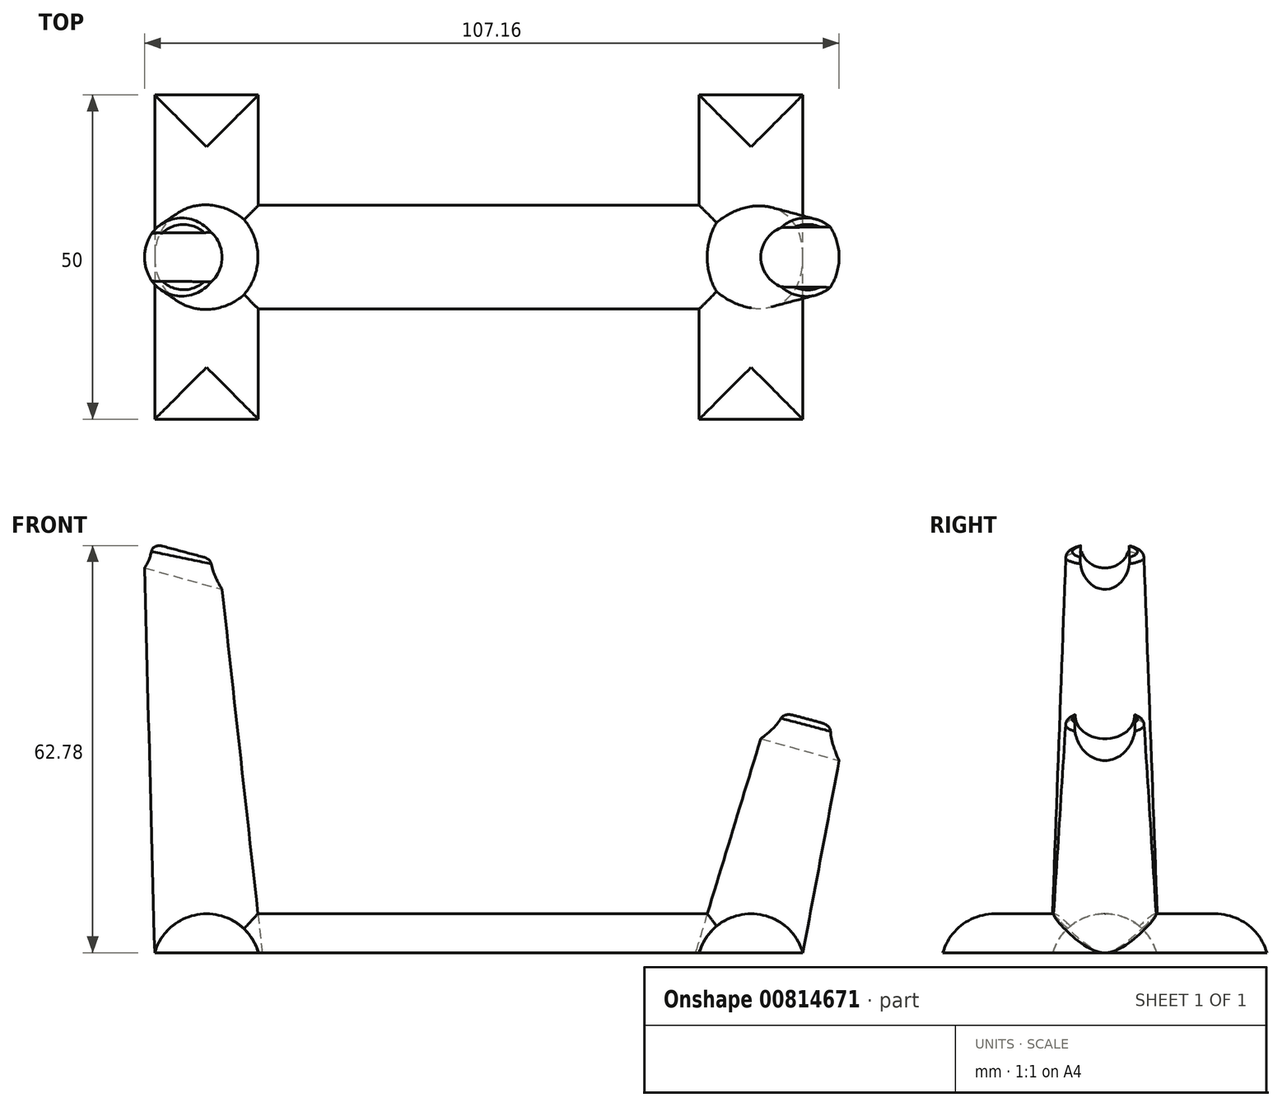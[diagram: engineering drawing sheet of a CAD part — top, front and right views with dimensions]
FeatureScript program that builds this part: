
annotation { "Feature Type Name" : "Feature", "Feature Type Description" : "" }
export const myFeature = defineFeature(function(context is Context, id is Id, definition is map)
    precondition{}
    {
        {
            var Q0;
            Q0=qCreatedBy(makeId("Top.planeOp"),FACE);
            var sketch = newSketch(context, id + "F0", { "sketchPlane" : qUnion([Q0])});
            skLineSegment(sketch, "E0.bottom", {"start": v(-50, 8) * mm, "end": v(50, 8) * mm});
            skLineSegment(sketch, "E0.top", {"start": v(-50, -8) * mm, "end": v(50, -8) * mm});
            skLineSegment(sketch, "E0.left", {"start": v(-50, 8) * mm, "end": v(-50, -8) * mm});
            skLineSegment(sketch, "E0.right", {"start": v(50, 8) * mm, "end": v(50, -8) * mm});
            skPoint(sketch, "E0.middle", {"position": v(0, 0) * mm});
            skLineSegment(sketch, "E1.bottom", {"start": v(-50, 25) * mm, "end": v(-34, 25) * mm});
            skLineSegment(sketch, "E1.top", {"start": v(-50, -25) * mm, "end": v(-34, -25) * mm});
            skLineSegment(sketch, "E1.left", {"start": v(-50, 25) * mm, "end": v(-50, -25) * mm});
            skLineSegment(sketch, "E1.right", {"start": v(-34, 25) * mm, "end": v(-34, -25) * mm});
            skLineSegment(sketch, "E2.bottom", {"start": v(50, -25) * mm, "end": v(34, -25) * mm});
            skLineSegment(sketch, "E2.top", {"start": v(50, 25) * mm, "end": v(34, 25) * mm});
            skLineSegment(sketch, "E2.left", {"start": v(50, -25) * mm, "end": v(50, 25) * mm});
            skLineSegment(sketch, "E2.right", {"start": v(34, -25) * mm, "end": v(34, 25) * mm});
            skPoint(sketch, "E3", {"position": v(-34, 0) * mm});
            skPoint(sketch, "E4", {"position": v(-50, 0) * mm});
            skPoint(sketch, "E5", {"position": v(34, 0) * mm});
            skSolve(sketch);
        }
        {
            var Q0;
            Q0 = qSketchRegion(id + "F0", true);
            extrude(context, id + "F1", {"entities" : qUnion([Q0]), "depth" : 6 * mm, "offsetDistance" : 25 * mm});
        }
        {
            var Q0;
            Q0=makeQuery(id+"F1.opExtrude","CAP_FACE",FACE,{"disambiguationData":[OSD([sQuery(id+"F0.wireOp",EDGE,"E0.bottom"),sQuery(id+"F0.wireOp",EDGE,"E0.top"),sQuery(id+"F0.wireOp",EDGE,"E1.bottom"),sQuery(id+"F0.wireOp",EDGE,"E1.top"),sQuery(id+"F0.wireOp",EDGE,"E1.left"),sQuery(id+"F0.wireOp",EDGE,"E1.right"),sQuery(id+"F0.wireOp",EDGE,"E2.bottom"),sQuery(id+"F0.wireOp",EDGE,"E2.top"),sQuery(id+"F0.wireOp",EDGE,"E2.left"),sQuery(id+"F0.wireOp",EDGE,"E2.right")])],"isStart":false});
            fillet(context, id + "F2", {"entities" : qUnion([Q0]), "radius" : 8.3 * mm, "tangentPropagation" : true, "allowEdgeOverflow" : false});
        }
        {
            var Q0;
            {var subQ0=sQuery(id+"F0.wireOp",EDGE,"E2.left");Q0=makeQuery(id+"F2.opFillet","BLEND_EDGE",EDGE,{"blendedFrom":[makeQuery(id+"F1.opExtrude","CAP_EDGE",EDGE,{"disambiguationData":[OSD([subQ0])],"isStart":false}),makeQuery(id+"F1.opExtrude","CAP_FACE",FACE,{"disambiguationData":[OSD([sQuery(id+"F0.wireOp",EDGE,"E0.bottom"),sQuery(id+"F0.wireOp",EDGE,"E0.top"),sQuery(id+"F0.wireOp",EDGE,"E1.bottom"),sQuery(id+"F0.wireOp",EDGE,"E1.top"),sQuery(id+"F0.wireOp",EDGE,"E1.left"),sQuery(id+"F0.wireOp",EDGE,"E1.right"),sQuery(id+"F0.wireOp",EDGE,"E2.bottom"),sQuery(id+"F0.wireOp",EDGE,"E2.top"),subQ0,sQuery(id+"F0.wireOp",EDGE,"E2.right")])],"isStart":true})],"blendedInto":[makeQuery(id+"F1.opExtrude","CAP_FACE",FACE,{"disambiguationData":[OSD([sQuery(id+"F0.wireOp",EDGE,"E0.bottom"),sQuery(id+"F0.wireOp",EDGE,"E0.top"),sQuery(id+"F0.wireOp",EDGE,"E1.bottom"),sQuery(id+"F0.wireOp",EDGE,"E1.top"),sQuery(id+"F0.wireOp",EDGE,"E1.left"),sQuery(id+"F0.wireOp",EDGE,"E1.right"),sQuery(id+"F0.wireOp",EDGE,"E2.bottom"),sQuery(id+"F0.wireOp",EDGE,"E2.top"),subQ0,sQuery(id+"F0.wireOp",EDGE,"E2.right")])],"isStart":true})]});}
            cPlane(context, id + "F3", {"entities" : qUnion([Q0]), "cplaneType" : CPlaneType.LINE_ANGLE, "offset" : 25 * mm, "angle" : 15 * degree, "width" : 150 * mm, "height" : 150 * mm});
        }
        {
            var Q0;
            Q0=qCreatedBy(id+"F3.planeOp",FACE);
            cPlane(context, id + "F4", {"entities" : qUnion([Q0]), "cplaneType" : CPlaneType.OFFSET, "offset" : 35 * mm, "width" : 150 * mm, "height" : 150 * mm});
        }
        {
            var Q0;
            Q0=makeQuery(id+"F1.opExtrude","CAP_FACE",FACE,{"disambiguationData":[OSD([sQuery(id+"F0.wireOp",EDGE,"E0.bottom"),sQuery(id+"F0.wireOp",EDGE,"E0.top"),sQuery(id+"F0.wireOp",EDGE,"E1.bottom"),sQuery(id+"F0.wireOp",EDGE,"E1.top"),sQuery(id+"F0.wireOp",EDGE,"E1.left"),sQuery(id+"F0.wireOp",EDGE,"E1.right"),sQuery(id+"F0.wireOp",EDGE,"E2.bottom"),sQuery(id+"F0.wireOp",EDGE,"E2.top"),sQuery(id+"F0.wireOp",EDGE,"E2.left"),sQuery(id+"F0.wireOp",EDGE,"E2.right")])],"isStart":true});
            var sketch = newSketch(context, id + "F5", { "sketchPlane" : qUnion([Q0])});
            skCircle(sketch, "E6", {"center": v(-41.7, 0) * mm, "radius": 8.3 * mm});
            skCircle(sketch, "E7", {"center": v(41.7, 0) * mm, "radius": 8.3 * mm});
            skPoint(sketch, "E8", {"position": v(-50, 0) * mm});
            skPoint(sketch, "E9", {"position": v(50, 0) * mm});
            skSolve(sketch);
        }
        {
            var Q0;
            Q0=qCreatedBy(id+"F4.planeOp",FACE);
            var sketch = newSketch(context, id + "F6", { "sketchPlane" : qUnion([Q0])});
            skCircle(sketch, "E10", {"center": v(-60.35, 0) * mm, "radius": 6 * mm});
            skCircle(sketch, "E11", {"center": v(39.65, 0) * mm, "radius": 6 * mm});
            skPoint(sketch, "E12", {"position": v(-66.35, 0) * mm});
            skPoint(sketch, "E13", {"position": v(45.65, 0) * mm});
            skLineSegment(sketch, "E14", {"start": v(-60.35, 0) * mm, "end": v(-10.35, 0) * mm, "construction": true});
            skLineSegment(sketch, "E15", {"start": v(-10.35, 0) * mm, "end": v(39.65, 0) * mm, "construction": true});
            skSolve(sketch);
        }
        {
            var Q1;
            Q1=makeQuery(id+"F6.imprint","IMPRINT",FACE,{"disambiguationData":[TD([[makeQuery(id+"F6.imprint","IMPRINT",EDGE,{"derivedFrom":sQuery(id+"F6.wireOp",EDGE,"E10")}),1.0]])]});
            var Q2;
            Q2=makeQuery(id+"F5.imprint","IMPRINT",FACE,{"disambiguationData":[TD([[makeQuery(id+"F5.imprint","IMPRINT",EDGE,{"derivedFrom":sQuery(id+"F5.wireOp",EDGE,"E6")}),1.0]])]});
            var Q3;
            Q3=sQuery(id+"F5.wireOp",VERTEX,"E8");
            var Q4;
            Q4=sQuery(id+"F6.wireOp",VERTEX,"E12");
            loft(context, id + "F7", {"operationType" : NewBodyOperationType.ADD, "sheetProfilesArray" : [{ "sheetProfileEntities" : qUnion([Q1]) }, { "sheetProfileEntities" : qUnion([Q2]) }], "matchConnections" : true, "connections" : [{ "connectionEntities" : qUnion([Q3, Q4]), "connectionEdgeQueries" : qUnion([]), "connectionEdgeParameters" : [] }]});
        }
        {
            var Q1;
            Q1=makeQuery(id+"F6.imprint","IMPRINT",FACE,{"disambiguationData":[TD([[makeQuery(id+"F6.imprint","IMPRINT",EDGE,{"derivedFrom":sQuery(id+"F6.wireOp",EDGE,"E11")}),1.0]])]});
            var Q2;
            Q2=makeQuery(id+"F5.imprint","IMPRINT",FACE,{"disambiguationData":[TD([[makeQuery(id+"F5.imprint","IMPRINT",EDGE,{"derivedFrom":sQuery(id+"F5.wireOp",EDGE,"E7")}),1.0]])]});
            var Q3;
            Q3=sQuery(id+"F5.wireOp",VERTEX,"E9");
            var Q4;
            Q4=sQuery(id+"F6.wireOp",VERTEX,"E13");
            loft(context, id + "F8", {"operationType" : NewBodyOperationType.ADD, "sheetProfilesArray" : [{ "sheetProfileEntities" : qUnion([Q1]) }, { "sheetProfileEntities" : qUnion([Q2]) }], "matchConnections" : true, "connections" : [{ "connectionEntities" : qUnion([Q3, Q4]), "connectionEdgeQueries" : qUnion([]), "connectionEdgeParameters" : [] }]});
        }
        {
            var Q0;
            Q0=makeQuery(id+"F7.opLoft","CAP_FACE",FACE,{"disambiguationData":[OSD([makeQuery(id+"F6.imprint","IMPRINT",FACE,{"disambiguationData":[TD([[makeQuery(id+"F6.imprint","IMPRINT",EDGE,{"derivedFrom":sQuery(id+"F6.wireOp",EDGE,"E10")}),1.0]])]})])],"isStart":true});
            var sketch = newSketch(context, id + "F9", { "sketchPlane" : qUnion([Q0])});
            skLineSegment(sketch, "E16.bottom", {"start": v(35.97, 4.74) * mm, "end": v(54.64, 4.74) * mm});
            skLineSegment(sketch, "E16.top", {"start": v(35.97, -4.79) * mm, "end": v(54.64, -4.79) * mm});
            skLineSegment(sketch, "E16.left", {"start": v(35.97, 4.74) * mm, "end": v(35.97, -4.79) * mm});
            skLineSegment(sketch, "E16.right", {"start": v(54.64, 4.74) * mm, "end": v(54.64, -4.79) * mm});
            skPoint(sketch, "E17", {"position": v(35.97, -0.03) * mm});
            skLineSegment(sketch, "E18.bottom", {"start": v(35.97, 4.74) * mm, "end": v(31.93, 4.74) * mm});
            skLineSegment(sketch, "E18.top", {"start": v(35.97, -4.79) * mm, "end": v(31.93, -4.79) * mm});
            skLineSegment(sketch, "E18.right", {"start": v(31.93, 4.74) * mm, "end": v(31.93, -4.79) * mm});
            skLineSegment(sketch, "E19.bottom", {"start": v(-55.64, 3.72) * mm, "end": v(-81.84, 3.72) * mm});
            skLineSegment(sketch, "E19.top", {"start": v(-55.64, -3.77) * mm, "end": v(-81.84, -3.77) * mm});
            skLineSegment(sketch, "E19.left", {"start": v(-55.64, 3.72) * mm, "end": v(-55.64, -3.77) * mm});
            skLineSegment(sketch, "E19.right", {"start": v(-81.84, 3.72) * mm, "end": v(-81.84, -3.77) * mm});
            skLineSegment(sketch, "E20.bottom", {"start": v(-60.2, 3.72) * mm, "end": v(-55.64, 3.72) * mm});
            skLineSegment(sketch, "E20.top", {"start": v(-60.2, -3.77) * mm, "end": v(-55.64, -3.77) * mm});
            skLineSegment(sketch, "E20.right", {"start": v(-60.2, 3.72) * mm, "end": v(-60.2, -3.77) * mm});
            skPoint(sketch, "E21", {"position": v(-81.84, -0.03) * mm});
            skSolve(sketch);
        }
        {
            var Q0;
            Q0=sQuery(id+"F9.wireOp",EDGE,"E16.right");
            cPlane(context, id + "F10", {"entities" : qUnion([Q0]), "cplaneType" : CPlaneType.LINE_ANGLE, "offset" : 25 * mm, "angle" : 75 * degree, "width" : 150 * mm, "height" : 150 * mm});
        }
        {
            var Q0;
            Q0=qCreatedBy(id+"F10.planeOp",FACE);
            var sketch = newSketch(context, id + "F11", { "sketchPlane" : qUnion([Q0])});
            skCircle(sketch, "E22", {"center": v(0, 47.7) * mm, "radius": 4.76 * mm});
            skSolve(sketch);
        }
        {
            var Q0;
            Q0 = qSketchRegion(id + "F11", true);
            extrude(context, id + "F12", {"entities" : qUnion([Q0]), "operationType" : NewBodyOperationType.REMOVE, "endBound" : BoundingType.THROUGH_ALL, "oppositeDirection" : true, "depth" : 200 * mm, "offsetDistance" : 25 * mm, "hasDraft" : true, "draftAngle" : .5 * degree, "draftPullDirection" : true, "hasSecondDirection" : true, "secondDirectionOppositeDirection" : false, "secondDirectionDepth" : 25 * mm});
        }
        {
            var Q0;
            Q0=makeQuery(id+"F12.boolean.opBoolean","SPLIT",EDGE,{"disambiguationData":[OD(0.0)],"derivedFrom":makeQuery(id+"F7.opLoft","MID_CAP_EDGE",EDGE,{"disambiguationData":[OSD([sQuery(id+"F6.wireOp",VERTEX,"E12"),sQuery(id+"F6.wireOp",EDGE,"E10")])],"capPos":0.0})});
            var Q1;
            Q1=makeQuery(id+"F12.boolean.opBoolean","SPLIT",EDGE,{"disambiguationData":[OD(1.0)],"derivedFrom":makeQuery(id+"F7.opLoft","MID_CAP_EDGE",EDGE,{"disambiguationData":[OSD([sQuery(id+"F6.wireOp",VERTEX,"E12"),sQuery(id+"F6.wireOp",EDGE,"E10")])],"capPos":0.0})});
            var Q2;
            Q2=makeQuery(id+"F12.boolean.opBoolean","SPLIT",EDGE,{"disambiguationData":[OD(0.0)],"derivedFrom":makeQuery(id+"F8.opLoft","MID_CAP_EDGE",EDGE,{"disambiguationData":[OSD([sQuery(id+"F6.wireOp",VERTEX,"E13"),sQuery(id+"F6.wireOp",EDGE,"E11")])],"capPos":0.0})});
            var Q3;
            Q3=makeQuery(id+"F12.boolean.opBoolean","SPLIT",EDGE,{"disambiguationData":[OD(1.0)],"derivedFrom":makeQuery(id+"F8.opLoft","MID_CAP_EDGE",EDGE,{"disambiguationData":[OSD([sQuery(id+"F6.wireOp",VERTEX,"E13"),sQuery(id+"F6.wireOp",EDGE,"E11")])],"capPos":0.0})});
            fillet(context, id + "F13", {"entities" : qUnion([Q0, Q1, Q2, Q3]), "radius" : 1 * mm, "tangentPropagation" : true, "allowEdgeOverflow" : false});
        }
    });
